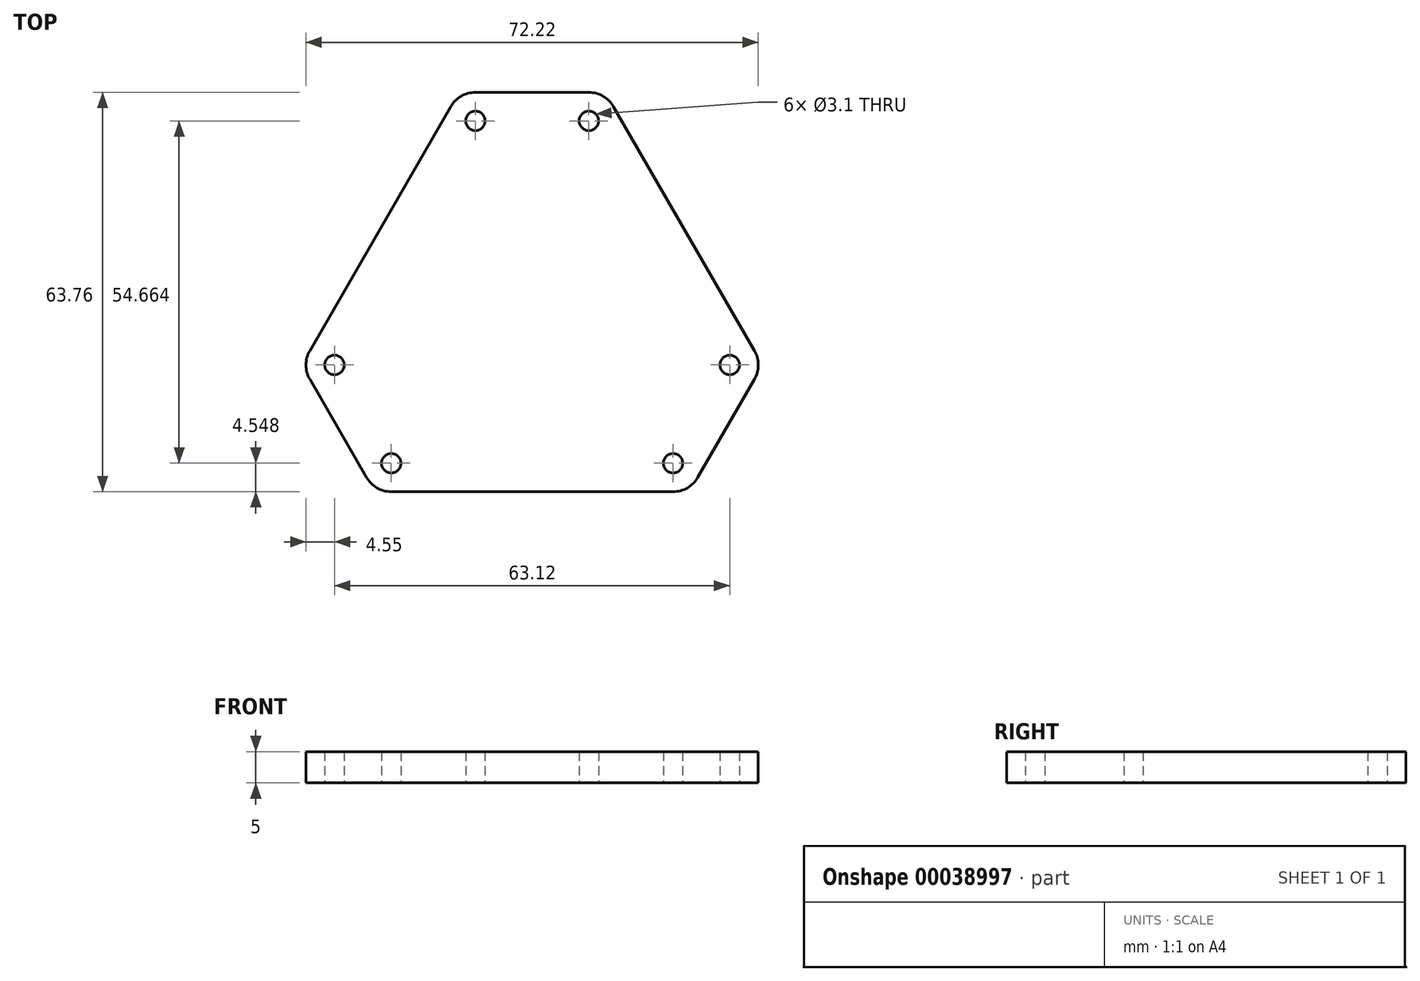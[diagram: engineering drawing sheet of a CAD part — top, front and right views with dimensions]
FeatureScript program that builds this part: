
annotation { "Feature Type Name" : "Feature", "Feature Type Description" : "" }
export const myFeature = defineFeature(function(context is Context, id is Id, definition is map)
    precondition{}
    {
        {
            var Q0;
            Q0=qCreatedBy(makeId("Top.planeOp"),FACE);
            var sketch = newSketch(context, id + "F0", { "sketchPlane" : qUnion([Q0])});
            skCircle(sketch, "E0", {"center": v(-22.5, -23.45) * mm, "radius": 1.55 * mm});
            skCircle(sketch, "E1", {"center": v(22.5, -23.45) * mm, "radius": 1.55 * mm});
            skLineSegment(sketch, "E2", {"start": v(-22.5, -23.45) * mm, "end": v(22.5, -23.45) * mm, "construction": true});
            skLineSegment(sketch, "E3", {"start": v(0, 0) * mm, "end": v(0, -23.45) * mm, "construction": true});
            skCircle(sketch, "E4", {"center": v(0, 0) * mm, "radius": 32.5 * mm, "construction": true});
            skLineSegment(sketch, "E5", {"start": v(-22.5, -28) * mm, "end": v(22.5, -28) * mm});
            skPoint(sketch, "E6.visualSharp", {"position": v(-33.76, -28) * mm});
            skPoint(sketch, "E7.visualSharp", {"position": v(33.76, -28) * mm});
            skArc(sketch, "E7.filletArc", {"start": v(22.5, -28) * mm, "mid": v(24.77, -27.4) * mm, "end": v(26.44, -25.73) * mm});
            skPoint(sketch, "E8.endSnap0", {"position": v(12.51, -10.17) * mm});
            skLineSegment(sketch, "E9", {"start": v(-26.44, -25.73) * mm, "end": v(-30.97, -17.88) * mm});
            skLineSegment(sketch, "E10", {"start": v(-30.97, -17.88) * mm, "end": v(0, 0) * mm});
            skLineSegment(sketch, "E11", {"start": v(0, 0) * mm, "end": v(30.97, -17.88) * mm});
            skLineSegment(sketch, "E12", {"start": v(30.97, -17.88) * mm, "end": v(26.44, -25.73) * mm});
            skPoint(sketch, "E12.endSnap0", {"position": v(26.44, -25.73) * mm});
            skArc(sketch, "E13.trimOffspring", {"start": v(-26.44, -25.73) * mm, "mid": v(-24.77, -27.4) * mm, "end": v(-22.5, -28) * mm});
            skSolve(sketch);
        }
        {
            var Q0;
            Q0 = qSketchRegion(id + "F0", true);
            extrude(context, id + "F1", {"entities" : qUnion([Q0]), "depth" : 5 * mm});
        }
        {
            var Q0;
            Q0=makeQuery(id+"F1.opExtrude","SWEPT_BODY",BODY,{"disambiguationData":[OSD([sQuery(id+"F0.wireOp",EDGE,"E0"),sQuery(id+"F0.wireOp",EDGE,"E1"),sQuery(id+"F0.wireOp",EDGE,"E5"),sQuery(id+"F0.wireOp",EDGE,"E7.filletArc"),sQuery(id+"F0.wireOp",EDGE,"E9"),sQuery(id+"F0.wireOp",EDGE,"E10"),sQuery(id+"F0.wireOp",EDGE,"E11"),sQuery(id+"F0.wireOp",EDGE,"E12"),sQuery(id+"F0.wireOp",EDGE,"E13.trimOffspring")])]});
            var Q1;
            Q1=makeQuery(id+"F1.opExtrude","SWEPT_EDGE",EDGE,{"disambiguationData":[OSD([sQuery(id+"F0.wireOp",EDGE,"E10"),sQuery(id+"F0.wireOp",EDGE,"E11")])]});
            circularPattern(context, id + "F2", {"operationType" : NewBodyOperationType.ADD, "entities" : qUnion([Q0]), "axis" : qUnion([Q1]), "angle" : 120 * degree, "instanceCount" : 3, "computeTransformsWithoutBuiltin" : true});
        }
    });
